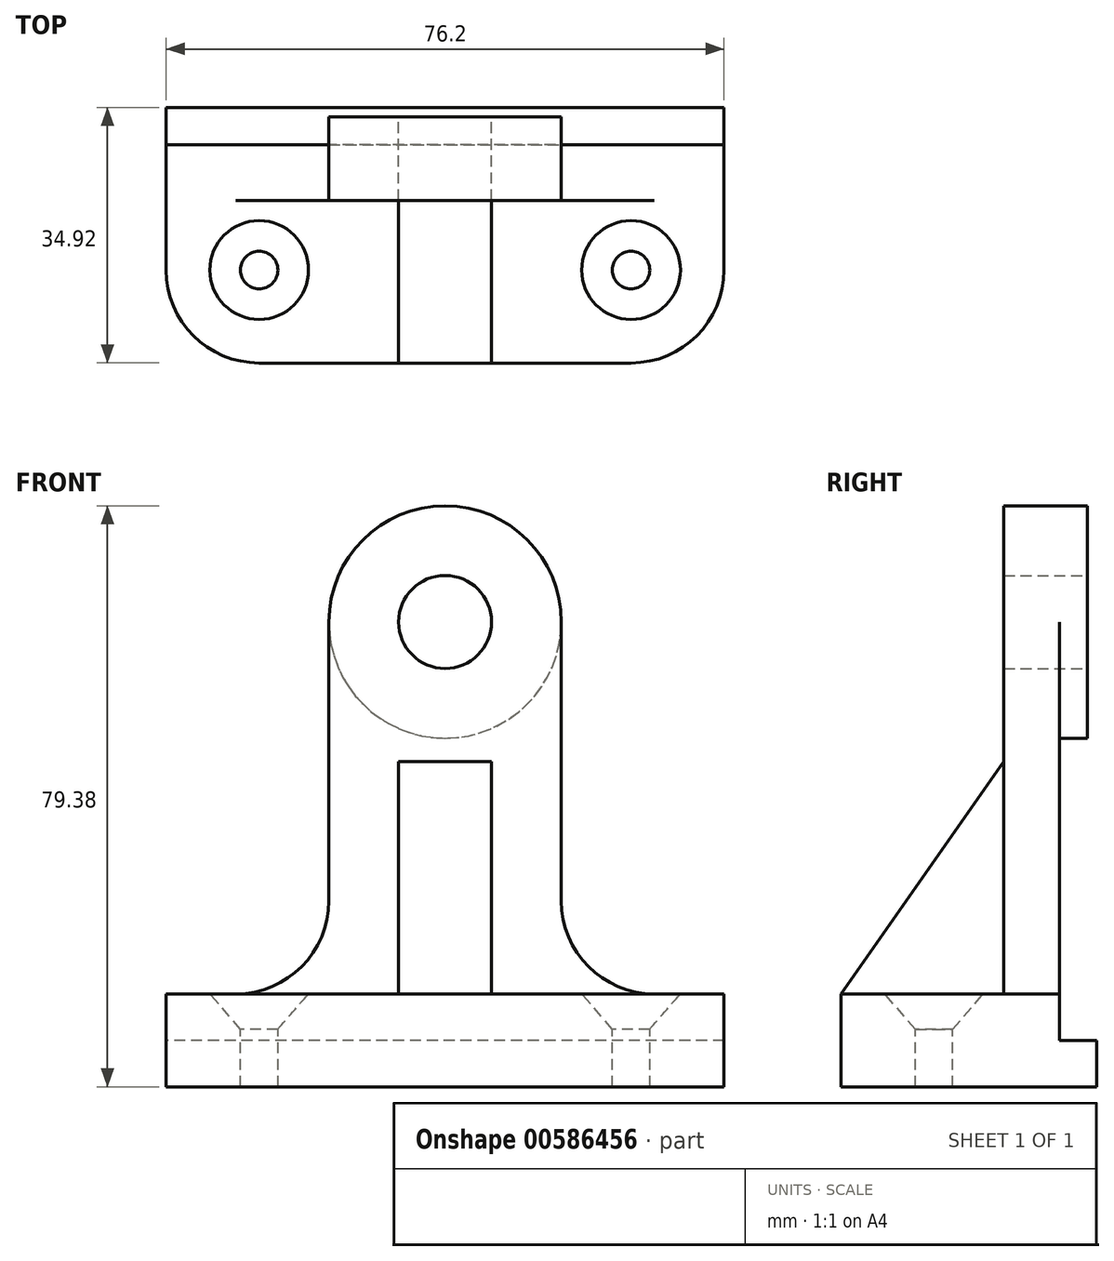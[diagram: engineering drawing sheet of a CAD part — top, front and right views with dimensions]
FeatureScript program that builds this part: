
annotation { "Feature Type Name" : "Feature", "Feature Type Description" : "" }
export const myFeature = defineFeature(function(context is Context, id is Id, definition is map)
    precondition{}
    {
        {
            var Q0;
            Q0=qCreatedBy(makeId("Front.planeOp"),FACE);
            var sketch = newSketch(context, id + "F0", { "sketchPlane" : qUnion([Q0])});
            skArc(sketch, "E0", {"start": v(15.88, 0) * mm, "mid": v(0, 15.88) * mm, "end": v(-15.88, 0) * mm});
            skCircle(sketch, "E1", {"center": v(0, 0) * mm, "radius": 6.35 * mm});
            skLineSegment(sketch, "E2", {"start": v(-38.1, -63.5) * mm, "end": v(38.1, -63.5) * mm});
            skLineSegment(sketch, "E3", {"start": v(0, 28.09) * mm, "end": v(0, -68.03) * mm, "construction": true});
            skPoint(sketch, "E3.endSnap0", {"position": v(0, -63.5) * mm});
            skLineSegment(sketch, "E4", {"start": v(-38.1, -63.5) * mm, "end": v(-38.1, -50.8) * mm});
            skLineSegment(sketch, "E5", {"start": v(-38.1, -50.8) * mm, "end": v(38.1, -50.8) * mm});
            skLineSegment(sketch, "E6", {"start": v(38.1, -50.8) * mm, "end": v(38.1, -63.5) * mm});
            skLineSegment(sketch, "E7", {"start": v(-15.88, 0) * mm, "end": v(-15.88, -38.1) * mm});
            skLineSegment(sketch, "E8", {"start": v(15.88, 0) * mm, "end": v(15.88, -38.1) * mm});
            skArc(sketch, "E9", {"start": v(-28.57, -50.8) * mm, "mid": v(-19.6, -47.08) * mm, "end": v(-15.87, -38.1) * mm});
            skArc(sketch, "E10", {"start": v(15.88, -38.1) * mm, "mid": v(19.6, -47.08) * mm, "end": v(28.58, -50.8) * mm});
            skSolve(sketch);
        }
        {
            var Q0;
            Q0=makeQuery(id+"F0.imprint","IMPRINT",FACE,{"disambiguationData":[TD([[makeQuery(id+"F0.imprint","IMPRINT",EDGE,{"derivedFrom":sQuery(id+"F0.wireOp",EDGE,"E2")}),1.0]])]});
            extrude(context, id + "F1", {"entities" : qUnion([Q0]), "depth" : 29.84 * mm, "offsetDistance" : 25.4 * mm});
        }
        {
            var Q0;
            Q0=makeQuery(id+"F0.imprint","IMPRINT",FACE,{"disambiguationData":[TD([[makeQuery(id+"F0.imprint","IMPRINT",EDGE,{"derivedFrom":sQuery(id+"F0.wireOp",EDGE,"E0")}),1.0]])]});
            extrude(context, id + "F2", {"entities" : qUnion([Q0]), "operationType" : NewBodyOperationType.ADD, "depth" : 7.62 * mm, "offsetDistance" : 25.4 * mm});
        }
        {
            var Q0;
            {var subQ0=sQuery(id+"F0.wireOp",EDGE,"E5");Q0=makeQuery(id+"F2.boolean.opBoolean","MERGE",FACE,{"derivedFrom":[makeQuery(id+"F1.opExtrude","CAP_FACE",FACE,{"disambiguationData":[OSD([sQuery(id+"F0.wireOp",EDGE,"E2"),sQuery(id+"F0.wireOp",EDGE,"E4"),subQ0,sQuery(id+"F0.wireOp",EDGE,"E6")])],"isStart":true}),makeQuery(id+"F2.opExtrude","CAP_FACE",FACE,{"disambiguationData":[OSD([sQuery(id+"F0.wireOp",EDGE,"E0"),sQuery(id+"F0.wireOp",EDGE,"E1"),subQ0,sQuery(id+"F0.wireOp",EDGE,"E7"),sQuery(id+"F0.wireOp",EDGE,"E8"),sQuery(id+"F0.wireOp",EDGE,"E9"),sQuery(id+"F0.wireOp",EDGE,"E10")])],"isStart":true})]});}
            var sketch = newSketch(context, id + "F3", { "sketchPlane" : qUnion([Q0])});
            skLineSegment(sketch, "E11.0", {"start": v(38.1, -63.5) * mm, "end": v(-38.1, -63.5) * mm});
            skLineSegment(sketch, "E12", {"start": v(-38.1, -63.5) * mm, "end": v(-38.1, -57.15) * mm});
            skLineSegment(sketch, "E13", {"start": v(-38.1, -57.15) * mm, "end": v(38.1, -57.15) * mm});
            skLineSegment(sketch, "E14", {"start": v(38.1, -57.15) * mm, "end": v(38.1, -63.5) * mm});
            skSolve(sketch);
        }
        {
            var Q0;
            Q0=makeQuery(id+"F3.imprint","IMPRINT",FACE,{"disambiguationData":[TD([[makeQuery(id+"F3.imprint","IMPRINT",EDGE,{"derivedFrom":sQuery(id+"F3.wireOp",EDGE,"E11.0")}),-1.0]])]});
            extrude(context, id + "F4", {"entities" : qUnion([Q0]), "operationType" : NewBodyOperationType.ADD, "depth" : 5.08 * mm, "offsetDistance" : 25.4 * mm});
        }
        {
            var Q0;
            {var subQ0=sQuery(id+"F0.wireOp",EDGE,"E5");Q0=makeQuery(id+"F2.boolean.opBoolean","MERGE",FACE,{"derivedFrom":[makeQuery(id+"F1.opExtrude","CAP_FACE",FACE,{"disambiguationData":[OSD([sQuery(id+"F0.wireOp",EDGE,"E2"),sQuery(id+"F0.wireOp",EDGE,"E4"),subQ0,sQuery(id+"F0.wireOp",EDGE,"E6")])],"isStart":true}),makeQuery(id+"F2.opExtrude","CAP_FACE",FACE,{"disambiguationData":[OSD([sQuery(id+"F0.wireOp",EDGE,"E0"),sQuery(id+"F0.wireOp",EDGE,"E1"),subQ0,sQuery(id+"F0.wireOp",EDGE,"E7"),sQuery(id+"F0.wireOp",EDGE,"E8"),sQuery(id+"F0.wireOp",EDGE,"E9"),sQuery(id+"F0.wireOp",EDGE,"E10")])],"isStart":true})]});}
            var sketch = newSketch(context, id + "F5", { "sketchPlane" : qUnion([Q0])});
            skArc(sketch, "E15.0", {"start": v(-15.88, 0) * mm, "mid": v(0, 15.88) * mm, "end": v(15.88, 0) * mm});
            skArc(sketch, "E16", {"start": v(-15.88, 0) * mm, "mid": v(0, -15.88) * mm, "end": v(15.88, 0) * mm});
            skCircle(sketch, "E17.0", {"center": v(0, 0) * mm, "radius": 6.35 * mm});
            skSolve(sketch);
        }
        {
            var Q0;
            Q0=makeQuery(id+"F5.imprint","IMPRINT",FACE,{"disambiguationData":[TD([[makeQuery(id+"F5.imprint","IMPRINT",EDGE,{"derivedFrom":sQuery(id+"F5.wireOp",EDGE,"E15.0")}),-1.0]])]});
            extrude(context, id + "F6", {"entities" : qUnion([Q0]), "operationType" : NewBodyOperationType.ADD, "depth" : 3.8 * mm, "offsetDistance" : 25.4 * mm});
        }
        {
            var Q0;
            Q0=qCreatedBy(makeId("Right.planeOp"),FACE);
            var sketch = newSketch(context, id + "F7", { "sketchPlane" : qUnion([Q0])});
            skLineSegment(sketch, "E18", {"start": v(-7.62, -19.05) * mm, "end": v(-29.85, -50.8) * mm});
            skLineSegment(sketch, "E19", {"start": v(-29.85, -50.8) * mm, "end": v(-7.62, -50.8) * mm});
            skLineSegment(sketch, "E20", {"start": v(-7.62, -50.8) * mm, "end": v(-7.62, -19.05) * mm});
            skSolve(sketch);
        }
        {
            var Q0;
            Q0 = qSketchRegion(id + "F7", true);
            extrude(context, id + "F8", {"entities" : qUnion([Q0]), "operationType" : NewBodyOperationType.ADD, "endBound" : BoundingType.SYMMETRIC, "depth" : 12.7 * mm, "offsetDistance" : 25.4 * mm});
        }
        {
            var Q0;
            Q0=makeQuery(id+"F1.opExtrude","CAP_EDGE",EDGE,{"disambiguationData":[OSD([sQuery(id+"F0.wireOp",EDGE,"E4")])],"isStart":false});
            var Q1;
            Q1=makeQuery(id+"F1.opExtrude","CAP_EDGE",EDGE,{"disambiguationData":[OSD([sQuery(id+"F0.wireOp",EDGE,"E6")])],"isStart":false});
            fillet(context, id + "F9", {"entities" : qUnion([Q0, Q1]), "radius" : 12.7 * mm, "tangentPropagation" : true, "allowEdgeOverflow" : false});
        }
        {
            var Q0;
            {var subQ0=sQuery(id+"F0.wireOp",EDGE,"E6");var subQ5=sQuery(id+"F0.wireOp",EDGE,"E5");Q0=makeQuery(id+"F8.boolean.opBoolean","SPLIT",FACE,{"disambiguationData":[TD([makeQuery(id+"F1.opExtrude","SWEPT_FACE",FACE,{"disambiguationData":[OSD([subQ0])]})])],"derivedFrom":makeQuery(id+"F1.opExtrude","SWEPT_FACE",FACE,{"disambiguationData":[OSD([subQ5])]})});}
            var sketch = newSketch(context, id + "F10", { "sketchPlane" : qUnion([Q0])});
            skLineSegment(sketch, "E21", {"start": v(25.4, -17.15) * mm, "end": v(-25.4, -17.15) * mm, "construction": true});
            skSolve(sketch);
        }
        {
            var Q0;
            Q0=sQuery(id+"F10.wireOp",VERTEX,"E21.start");
            var Q1;
            Q1=sQuery(id+"F10.wireOp",VERTEX,"E21.end");
            var Q2;
            Q2=makeQuery(id+"F1.opExtrude","SWEPT_BODY",BODY,{"disambiguationData":[OSD([sQuery(id+"F0.wireOp",EDGE,"E2"),sQuery(id+"F0.wireOp",EDGE,"E4"),sQuery(id+"F0.wireOp",EDGE,"E5"),sQuery(id+"F0.wireOp",EDGE,"E6")])]});
            hole(context, id + "F11", {"style" : HoleStyle.C_SINK, "endStyle" : HoleEndStyle.THROUGH, "standardTappedOrClearance" : lookupTablePath({ "standard" : "ANSI", "engagement" : "75%", "pitch" : "20 tpi", "size" : "1/4", "type" : "Tapped" }), "standardBlindInLast" : lookupTablePath({ "standard" : "ANSI", "engagement" : "75%", "pitch" : "20 tpi", "size" : "1/4", "type" : "Tapped" }), "holeDiameter" : 5.1 * mm, "cSinkDiameter" : 13.5 * mm, "cSinkAngle" : 82 * degree, "majorDiameter" : 6.35 * mm, "showTappedDepth" : true, "isTappedThrough" : true, "tappedDepth" : 72.44 * mm, "tapClearance" : 3, "startFromSketch" : true, "locations" : qUnion([Q0, Q1]), "scope" : qUnion([Q2])});
        }
    });
